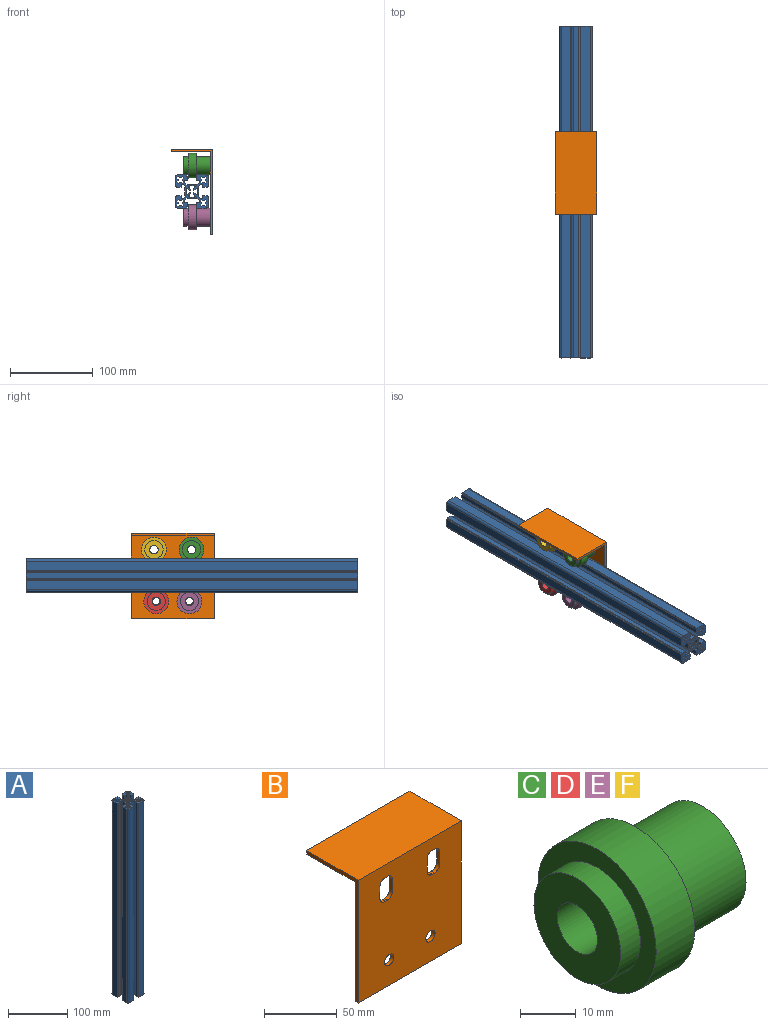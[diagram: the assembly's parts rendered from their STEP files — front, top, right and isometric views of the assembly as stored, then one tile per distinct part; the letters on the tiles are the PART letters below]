
ASSEMBLY  parts=6 mates=5
PART A: 178 faces, bbox 40x40x400 mm
  f0: cylinder r=2.77mm len=400mm, axis (0,0,1), area 706.3mm2, adj f1,f2,f176,f177
  f1: plane 400x1.43mm, normal (0.71,0.71,0), area 809.2mm2, adj f0,f175,f176,f177
  f2: plane 400x1.43mm, normal (0.71,-0.71,0), area 808.9mm2, adj f0,f163,f176,f177
  f3: cylinder r=3mm len=400mm, axis (0,0,1), area 1885mm2, adj f4,f82,f176,f177
  f4: plane 400x10.93mm, normal (-1,0,0), area 4370mm2, adj f3,f9,f176,f177
  f5: plane 400x3.65mm, normal (1,0,0), area 1460mm2, adj f6,f7,f176,f177
  f6: plane 400x2.46mm, normal (0,-1,0), area 984.8mm2, adj f5,f10,f176,f177
  f7: plane 400x5.5mm, normal (0,-1,0), area 2200mm2, adj f5,f8,f176,f177
  f8: plane 400x0.98mm, normal (-1,0,0), area 390mm2, adj f7,f9,f176,f177
  f9: plane 400x1.5mm, normal (0,-1,0), area 600mm2, adj f4,f8,f176,f177
  f10: plane 400x2.83mm, normal (-0.71,-0.71,0), area 1598.1mm2, adj f6,f11,f176,f177
  f11: cylinder r=0.5mm len=400mm, axis (0,0,1), area 325.2mm2, adj f10,f12,f176,f177
  f12: cylinder r=2.3mm len=400mm, axis (0,0,1), area 774mm2, adj f11,f13,f176,f177
  f13: plane 400x6.97mm, normal (-1,0,0), area 2787.1mm2, adj f12,f14,f176,f177
  f14: cylinder r=2.3mm len=400mm, axis (0,0,1), area 774mm2, adj f13,f15,f176,f177
  f15: cylinder r=0.5mm len=400mm, axis (0,0,1), area 325.1mm2, adj f14,f16,f176,f177
  f16: plane 400x2.83mm, normal (-0.71,0.71,0), area 1598.4mm2, adj f15,f17,f176,f177
  f17: plane 400x2.46mm, normal (0,1,0), area 984.8mm2, adj f16,f18,f176,f177
  f18: plane 400x3.65mm, normal (1,0,0), area 1460mm2, adj f17,f19,f176,f177
  f19: plane 400x5.5mm, normal (0,1,0), area 2200mm2, adj f18,f20,f176,f177
  f20: plane 400x0.98mm, normal (-1,0,0), area 390mm2, adj f19,f21,f176,f177
  f21: plane 400x1.5mm, normal (0,1,0), area 600mm2, adj f20,f22,f176,f177
  f22: plane 400x10.93mm, normal (-1,0,0), area 4370mm2, adj f21,f23,f176,f177
  f23: cylinder r=3mm len=400mm, axis (0,0,1), area 1885mm2, adj f22,f24,f176,f177
  f24: plane 400x10.93mm, normal (0,-1,0), area 4370mm2, adj f23,f25,f176,f177
  f25: plane 400x1.5mm, normal (1,0,0), area 600mm2, adj f24,f26,f176,f177
  f26: plane 400x0.98mm, normal (0,-1,0), area 390mm2, adj f25,f27,f176,f177
  f27: plane 400x5.5mm, normal (1,0,0), area 2200mm2, adj f26,f28,f176,f177
  f28: plane 400x3.65mm, normal (0,1,0), area 1460mm2, adj f27,f29,f176,f177
  f29: plane 400x2.46mm, normal (1,0,0), area 985.2mm2, adj f28,f30,f176,f177
  f30: plane 400x2.83mm, normal (0.71,-0.71,0), area 1598.1mm2, adj f29,f31,f176,f177
  f31: cylinder r=0.5mm len=400mm, axis (0,0,1), area 325.2mm2, adj f30,f32,f176,f177
  f32: cylinder r=2.3mm len=400mm, axis (0,0,1), area 774.5mm2, adj f31,f33,f176,f177
  f33: plane 400x6.97mm, normal (0,-1,0), area 2786.4mm2, adj f32,f34,f176,f177
  f34: cylinder r=2.3mm len=400mm, axis (0,0,1), area 774.5mm2, adj f33,f35,f176,f177
  f35: cylinder r=0.5mm len=400mm, axis (0,0,1), area 325.4mm2, adj f34,f36,f176,f177
  f36: plane 400x2.83mm, normal (-0.71,-0.71,0), area 1598.3mm2, adj f35,f37,f176,f177
  f37: plane 400x2.46mm, normal (-1,0,0), area 985.2mm2, adj f36,f38,f176,f177
  f38: plane 400x3.65mm, normal (0,1,0), area 1460mm2, adj f37,f39,f176,f177
  f39: plane 400x5.5mm, normal (-1,0,0), area 2200mm2, adj f38,f40,f176,f177
  f40: plane 400x0.98mm, normal (0,-1,0), area 390mm2, adj f39,f41,f176,f177
  f41: plane 400x1.5mm, normal (-1,0,0), area 600mm2, adj f40,f42,f176,f177
  f42: plane 400x10.93mm, normal (0,-1,0), area 4370mm2, adj f41,f43,f176,f177
  f43: cylinder r=3mm len=400mm, axis (0,0,1), area 1885mm2, adj f42,f44,f176,f177
  f44: plane 400x10.93mm, normal (1,0,0), area 4370mm2, adj f43,f45,f176,f177
  f45: plane 400x1.5mm, normal (0,1,0), area 600mm2, adj f44,f46,f176,f177
  f46: plane 400x0.98mm, normal (1,0,0), area 390mm2, adj f45,f47,f176,f177
  f47: plane 400x5.5mm, normal (0,1,0), area 2200mm2, adj f46,f48,f176,f177
  f48: plane 400x3.65mm, normal (-1,0,0), area 1460mm2, adj f47,f49,f176,f177
  f49: plane 400x2.46mm, normal (0,1,0), area 984.8mm2, adj f48,f50,f176,f177
  f50: plane 400x2.83mm, normal (0.71,0.71,0), area 1598.3mm2, adj f49,f51,f176,f177
  f51: cylinder r=0.5mm len=400mm, axis (0,0,1), area 325.4mm2, adj f50,f52,f176,f177
  f52: cylinder r=2.3mm len=400mm, axis (0,0,1), area 774mm2, adj f51,f53,f176,f177
  f53: plane 400x6.97mm, normal (1,0,0), area 2787.1mm2, adj f52,f54,f176,f177
  f54: cylinder r=2.3mm len=400mm, axis (0,0,1), area 774mm2, adj f53,f55,f176,f177
  f55: cylinder r=0.5mm len=400mm, axis (0,0,1), area 325.5mm2, adj f54,f56,f176,f177
  f56: plane 400x2.83mm, normal (0.71,-0.71,0), area 1598mm2, adj f55,f57,f176,f177
  f57: plane 400x2.46mm, normal (0,-1,0), area 984.8mm2, adj f56,f58,f176,f177
  f58: plane 400x3.65mm, normal (-1,0,0), area 1460mm2, adj f57,f59,f176,f177
  f59: plane 400x5.5mm, normal (0,-1,0), area 2200mm2, adj f58,f60,f176,f177
  f60: plane 400x0.98mm, normal (1,0,0), area 390mm2, adj f59,f61,f176,f177
  f61: plane 400x1.5mm, normal (0,-1,0), area 600mm2, adj f60,f62,f176,f177
  f62: plane 400x10.93mm, normal (1,0,0), area 4370mm2, adj f61,f63,f176,f177
  f63: cylinder r=3mm len=400mm, axis (0,0,1), area 1885mm2, adj f62,f64,f176,f177
  f64: plane 400x10.93mm, normal (0,1,0), area 4370mm2, adj f63,f65,f176,f177
  f65: plane 400x1.5mm, normal (-1,0,0), area 600mm2, adj f64,f66,f176,f177
  f66: plane 400x0.98mm, normal (0,1,0), area 390mm2, adj f65,f67,f176,f177
  f67: plane 400x5.5mm, normal (-1,0,0), area 2200mm2, adj f66,f68,f176,f177
  f68: plane 400x3.65mm, normal (0,-1,0), area 1460mm2, adj f67,f69,f176,f177
  f69: plane 400x2.46mm, normal (-1,0,0), area 984.8mm2, adj f68,f70,f176,f177
  f70: plane 400x2.83mm, normal (-0.71,0.71,0), area 1598.3mm2, adj f69,f71,f176,f177
  f71: cylinder r=0.5mm len=400mm, axis (0,0,1), area 325.4mm2, adj f70,f72,f176,f177
  f72: cylinder r=2.3mm len=400mm, axis (0,0,1), area 774mm2, adj f71,f73,f176,f177
  f73: plane 400x6.97mm, normal (0,1,0), area 2787.1mm2, adj f72,f74,f176,f177
  f74: cylinder r=2.3mm len=400mm, axis (0,0,1), area 774mm2, adj f73,f75,f176,f177
  f75: cylinder r=0.5mm len=400mm, axis (0,0,1), area 325.2mm2, adj f74,f76,f176,f177
  f76: plane 400x2.83mm, normal (0.71,0.71,0), area 1598.1mm2, adj f75,f77,f176,f177
  f77: plane 400x2.46mm, normal (1,0,0), area 984.8mm2, adj f76,f78,f176,f177
  f78: plane 400x3.65mm, normal (0,-1,0), area 1460mm2, adj f77,f79,f176,f177
  f79: plane 400x5.5mm, normal (1,0,0), area 2200mm2, adj f78,f80,f176,f177
  f80: plane 400x0.98mm, normal (0,1,0), area 390mm2, adj f79,f81,f176,f177
  f81: plane 400x1.5mm, normal (1,0,0), area 600mm2, adj f80,f82,f176,f177
  f82: plane 400x10.93mm, normal (0,1,0), area 4370mm2, adj f3,f81,f176,f177
  f83: plane 400x1.77mm, normal (0.71,0.71,0), area 999.8mm2, adj f84,f98,f176,f177
  f84: plane 400x1.43mm, normal (-0.71,0.71,0), area 808.9mm2, adj f83,f85,f176,f177
  f85: cylinder r=2.77mm len=400mm, axis (0,0,1), area 706.3mm2, adj f84,f86,f176,f177
  f86: plane 400x1.43mm, normal (0.71,0.71,0), area 808.9mm2, adj f85,f87,f176,f177
  f87: plane 400x1.77mm, normal (-0.71,0.71,0), area 999.8mm2, adj f86,f88,f176,f177
  f88: plane 400x1.43mm, normal (-0.71,-0.71,0), area 808.9mm2, adj f87,f89,f176,f177
  f89: cylinder r=2.77mm len=400mm, axis (0,0,1), area 706.3mm2, adj f88,f90,f176,f177
  f90: plane 400x1.43mm, normal (-0.71,0.71,0), area 809.2mm2, adj f89,f91,f176,f177
  f91: plane 400x1.77mm, normal (-0.71,-0.71,0), area 999.8mm2, adj f90,f92,f176,f177
  f92: plane 400x1.43mm, normal (0.71,-0.71,0), area 808.9mm2, adj f91,f93,f176,f177
  f93: cylinder r=2.77mm len=400mm, axis (0,0,1), area 706.3mm2, adj f92,f94,f176,f177
  f94: plane 400x1.43mm, normal (-0.71,-0.71,0), area 808.9mm2, adj f93,f95,f176,f177
  f95: plane 400x1.77mm, normal (0.71,-0.71,0), area 999.8mm2, adj f94,f96,f176,f177
  f96: plane 400x1.43mm, normal (0.71,0.71,0), area 809.2mm2, adj f95,f97,f176,f177
  f97: cylinder r=2.77mm len=400mm, axis (0,0,1), area 706.3mm2, adj f96,f98,f176,f177
  f98: plane 400x1.43mm, normal (0.71,-0.71,0), area 808.9mm2, adj f83,f97,f176,f177
  f99: plane 400x1.77mm, normal (0.71,0.71,0), area 999.8mm2, adj f100,f114,f176,f177
  f100: plane 400x1.43mm, normal (-0.71,0.71,0), area 808.9mm2, adj f99,f101,f176,f177
  f101: cylinder r=2.77mm len=400mm, axis (0,0,1), area 706.3mm2, adj f100,f102,f176,f177
  f102: plane 400x1.43mm, normal (0.71,0.71,0), area 808.9mm2, adj f101,f103,f176,f177
  f103: plane 400x1.77mm, normal (-0.71,0.71,0), area 999.8mm2, adj f102,f104,f176,f177
  f104: plane 400x1.43mm, normal (-0.71,-0.71,0), area 808.9mm2, adj f103,f105,f176,f177
  f105: cylinder r=2.77mm len=400mm, axis (0,0,1), area 706.3mm2, adj f104,f106,f176,f177
  f106: plane 400x1.43mm, normal (-0.71,0.71,0), area 809.2mm2, adj f105,f107,f176,f177
  f107: plane 400x1.77mm, normal (-0.71,-0.71,0), area 999.8mm2, adj f106,f108,f176,f177
  f108: plane 400x1.43mm, normal (0.71,-0.71,0), area 808.9mm2, adj f107,f109,f176,f177
  f109: cylinder r=2.77mm len=400mm, axis (0,0,1), area 706.3mm2, adj f108,f110,f176,f177
  f110: plane 400x1.43mm, normal (-0.71,-0.71,0), area 808.9mm2, adj f109,f111,f176,f177
  f111: plane 400x1.77mm, normal (0.71,-0.71,0), area 999.8mm2, adj f110,f112,f176,f177
  f112: plane 400x1.43mm, normal (0.71,0.71,0), area 809.2mm2, adj f111,f113,f176,f177
  f113: cylinder r=2.77mm len=400mm, axis (0,0,1), area 706.3mm2, adj f112,f114,f176,f177
  f114: plane 400x1.43mm, normal (0.71,-0.71,0), area 808.9mm2, adj f99,f113,f176,f177
  f115: cylinder r=1mm len=400mm, axis (0,0,1), area 942.5mm2, adj f116,f146,f176,f177
  f116: plane 400x0.99mm, normal (-0.71,0.71,0), area 560mm2, adj f115,f117,f176,f177
  f117: plane 400x1.58mm, normal (-0.57,0.82,0), area 769.1mm2, adj f116,f118,f176,f177
  f118: cylinder r=2.77mm len=400mm, axis (0,0,1), area 621mm2, adj f117,f119,f176,f177
  f119: plane 400x1.58mm, normal (0.82,-0.57,0), area 769.1mm2, adj f118,f120,f176,f177
  f120: plane 400x0.99mm, normal (0.71,-0.71,0), area 560.5mm2, adj f119,f121,f176,f177
  f121: cylinder r=1mm len=400mm, axis (0,0,1), area 942.5mm2, adj f120,f122,f176,f177
  f122: plane 400x5.46mm, normal (0,1,0), area 2184.6mm2, adj f121,f123,f176,f177
  f123: cylinder r=1mm len=400mm, axis (0,0,1), area 942.5mm2, adj f122,f124,f176,f177
  f124: plane 400x0.99mm, normal (-0.71,-0.71,0), area 560.5mm2, adj f123,f125,f176,f177
  f125: plane 400x1.58mm, normal (-0.82,-0.57,0), area 769.1mm2, adj f124,f126,f176,f177
  f126: cylinder r=2.77mm len=400mm, axis (0,0,1), area 620.7mm2, adj f125,f127,f176,f177
  f127: plane 400x1.58mm, normal (0.57,0.82,0), area 769.5mm2, adj f126,f128,f176,f177
  f128: plane 400x0.99mm, normal (0.71,0.71,0), area 560mm2, adj f127,f129,f176,f177
  f129: cylinder r=1mm len=400mm, axis (0,0,1), area 942.5mm2, adj f128,f130,f176,f177
  f130: plane 400x5.46mm, normal (-1,0,0), area 2184.2mm2, adj f129,f131,f176,f177
  f131: cylinder r=1mm len=400mm, axis (0,0,1), area 942.5mm2, adj f130,f132,f176,f177
  f132: plane 400x0.99mm, normal (0.71,-0.71,0), area 560mm2, adj f131,f133,f176,f177
  f133: plane 400x1.58mm, normal (0.57,-0.82,0), area 769.5mm2, adj f132,f134,f176,f177
  f134: cylinder r=2.77mm len=400mm, axis (0,0,1), area 620.7mm2, adj f133,f135,f176,f177
  f135: plane 400x1.58mm, normal (-0.82,0.57,0), area 769.1mm2, adj f134,f136,f176,f177
  f136: plane 400x0.99mm, normal (-0.71,0.71,0), area 560mm2, adj f135,f137,f176,f177
  f137: cylinder r=1mm len=400mm, axis (0,0,1), area 942.5mm2, adj f136,f138,f176,f177
  f138: plane 400x5.46mm, normal (0,-1,0), area 2183.8mm2, adj f137,f139,f176,f177
  f139: cylinder r=1mm len=400mm, axis (0,0,1), area 942.5mm2, adj f138,f140,f176,f177
  f140: plane 400x0.99mm, normal (0.71,0.71,0), area 560mm2, adj f139,f141,f176,f177
  f141: plane 400x1.58mm, normal (0.82,0.57,0), area 769.1mm2, adj f140,f142,f176,f177
  f142: cylinder r=2.77mm len=400mm, axis (0,0,1), area 621mm2, adj f141,f143,f176,f177
  f143: plane 400x1.58mm, normal (-0.57,-0.82,0), area 769.1mm2, adj f142,f144,f176,f177
  f144: plane 400x0.99mm, normal (-0.71,-0.71,0), area 560mm2, adj f143,f145,f176,f177
  f145: cylinder r=1mm len=400mm, axis (0,0,1), area 942.5mm2, adj f144,f146,f176,f177
  f146: plane 400x5.46mm, normal (1,0,0), area 2184.2mm2, adj f115,f145,f176,f177
  f147: plane 400x1.43mm, normal (0.71,0.71,0), area 809.2mm2, adj f148,f162,f176,f177
  f148: cylinder r=2.77mm len=400mm, axis (0,0,1), area 706.3mm2, adj f147,f149,f176,f177
  f149: plane 400x1.43mm, normal (0.71,-0.71,0), area 808.9mm2, adj f148,f150,f176,f177
  f150: plane 400x1.77mm, normal (0.71,0.71,0), area 999.8mm2, adj f149,f151,f176,f177
  f151: plane 400x1.43mm, normal (-0.71,0.71,0), area 808.9mm2, adj f150,f152,f176,f177
  f152: cylinder r=2.77mm len=400mm, axis (0,0,1), area 706.3mm2, adj f151,f153,f176,f177
  f153: plane 400x1.43mm, normal (0.71,0.71,0), area 808.9mm2, adj f152,f154,f176,f177
  f154: plane 400x1.77mm, normal (-0.71,0.71,0), area 999.8mm2, adj f153,f155,f176,f177
  f155: plane 400x1.43mm, normal (-0.71,-0.71,0), area 808.9mm2, adj f154,f156,f176,f177
  f156: cylinder r=2.77mm len=400mm, axis (0,0,1), area 706.3mm2, adj f155,f157,f176,f177
  f157: plane 400x1.43mm, normal (-0.71,0.71,0), area 809.2mm2, adj f156,f158,f176,f177
  f158: plane 400x1.77mm, normal (-0.71,-0.71,0), area 999.8mm2, adj f157,f159,f176,f177
  f159: plane 400x1.43mm, normal (0.71,-0.71,0), area 808.9mm2, adj f158,f160,f176,f177
  f160: cylinder r=2.77mm len=400mm, axis (0,0,1), area 706.3mm2, adj f159,f161,f176,f177
  f161: plane 400x1.43mm, normal (-0.71,-0.71,0), area 808.9mm2, adj f160,f162,f176,f177
  f162: plane 400x1.77mm, normal (0.71,-0.71,0), area 999.8mm2, adj f147,f161,f176,f177
  f163: plane 400x1.77mm, normal (0.71,0.71,0), area 999.8mm2, adj f2,f164,f176,f177
  f164: plane 400x1.43mm, normal (-0.71,0.71,0), area 808.9mm2, adj f163,f165,f176,f177
  f165: cylinder r=2.77mm len=400mm, axis (0,0,1), area 706.3mm2, adj f164,f166,f176,f177
  f166: plane 400x1.43mm, normal (0.71,0.71,0), area 808.9mm2, adj f165,f167,f176,f177
  f167: plane 400x1.77mm, normal (-0.71,0.71,0), area 999.8mm2, adj f166,f168,f176,f177
  f168: plane 400x1.43mm, normal (-0.71,-0.71,0), area 808.9mm2, adj f167,f169,f176,f177
  f169: cylinder r=2.77mm len=400mm, axis (0,0,1), area 706.3mm2, adj f168,f170,f176,f177
  f170: plane 400x1.43mm, normal (-0.71,0.71,0), area 809.2mm2, adj f169,f171,f176,f177
  f171: plane 400x1.77mm, normal (-0.71,-0.71,0), area 999.8mm2, adj f170,f172,f176,f177
  f172: plane 400x1.43mm, normal (0.71,-0.71,0), area 808.9mm2, adj f171,f173,f176,f177
  f173: cylinder r=2.77mm len=400mm, axis (0,0,1), area 706.3mm2, adj f172,f174,f176,f177
  f174: plane 400x1.43mm, normal (-0.71,-0.71,0), area 808.9mm2, adj f173,f175,f176,f177
  f175: plane 400x1.77mm, normal (0.71,-0.71,0), area 999.8mm2, adj f1,f174,f176,f177
  f176: plane 40x40mm, normal (0,0,1), area 698.5mm2, adj f0,f1,f2,f3,f4,f5,f6,f7
  f177: plane 40x40mm, normal (0,0,-1), area 698.5mm2, adj f0,f1,f2,f3,f4,f5,f6,f7
PART B: 26 faces, bbox 100x50x103 mm
  f0: plane 103x100mm, normal (0,-1,0), area 9727.7mm2, adj f2,f5,f6,f7,f8,f9,f10,f11
  f1: plane 100x100mm, normal (0,1,0), area 9427.7mm2, adj f2,f3,f6,f7,f8,f9,f10,f11
  f2: plane 100x3mm, normal (0,0,-1), area 300mm2, adj f0,f1,f6,f7
  f3: plane 100x47mm, normal (0,0,-1), area 4700mm2, adj f1,f4,f6,f7
  f4: plane 100x3mm, normal (0,1,0), area 300mm2, adj f3,f5,f6,f7
  f5: plane 100x50mm, normal (0,0,1), area 5000mm2, adj f0,f4,f6,f7
  f6: plane 103x50mm, normal (1,0,0), area 450mm2, adj f0,f1,f2,f3,f4,f5
  f7: plane 103x50mm, normal (-1,0,0), area 450mm2, adj f0,f1,f2,f3,f4,f5
  f8: plane 3x2.2mm, normal (0,0,-1), area 6.6mm2, adj f0,f1,f9,f15
  f9: cylinder r=5mm len=5mm, axis (0,-1,0), area 23.6mm2, adj f0,f1,f8,f10
  f10: plane 10x3mm, normal (1,0,0), area 30mm2, adj f0,f1,f9,f11
  f11: cylinder r=5mm len=5mm, axis (0,-1,0), area 23.6mm2, adj f0,f1,f10,f12
  f12: plane 3x2.2mm, normal (0,0,1), area 6.6mm2, adj f0,f1,f11,f13
  f13: cylinder r=5mm len=5mm, axis (0,-1,0), area 23.6mm2, adj f0,f1,f12,f14
  f14: plane 10x3mm, normal (-1,0,0), area 30mm2, adj f0,f1,f13,f15
  f15: cylinder r=5mm len=5mm, axis (0,-1,0), area 23.6mm2, adj f0,f1,f8,f14
  f16: cylinder r=5mm len=5mm, axis (0,-1,0), area 23.6mm2, adj f0,f1,f17,f23
  f17: plane 10x3mm, normal (1,0,0), area 30mm2, adj f0,f1,f16,f18
  f18: cylinder r=5mm len=5mm, axis (0,-1,0), area 23.6mm2, adj f0,f1,f17,f19
  f19: plane 3x2.2mm, normal (0,0,1), area 6.6mm2, adj f0,f1,f18,f20
  f20: cylinder r=5mm len=5mm, axis (0,-1,0), area 23.6mm2, adj f0,f1,f19,f21
  f21: plane 10x3mm, normal (-1,0,0), area 30mm2, adj f0,f1,f20,f22
  f22: cylinder r=5mm len=5mm, axis (0,-1,0), area 23.6mm2, adj f0,f1,f21,f23
  f23: plane 3x2.2mm, normal (0,0,-1), area 6.6mm2, adj f0,f1,f16,f22
  f24: cylinder r=4.5mm len=9mm, axis (0,-1,0), area 84.8mm2, adj f0,f1
  f25: cylinder r=4.5mm len=9mm, axis (0,-1,0), area 84.8mm2, adj f0,f1
PART C: 8 faces, bbox 31.8x30x30 mm
  f0: cylinder r=11mm len=22mm, axis (-1,0,0), area 1175mm2, adj f1,f6
  f1: plane 30x30mm, normal (1,0,0), area 326.7mm2, adj f0,f2
  f2: cylinder r=15mm len=30mm, axis (-1,0,0), area 923.6mm2, adj f1,f3
  f3: plane 30x30mm, normal (-1,0,0), area 326.7mm2, adj f2,f4
  f4: cylinder r=11mm len=22mm, axis (-1,0,0), area 345.6mm2, adj f3,f5
  f5: plane 22x22mm, normal (-1,0,0), area 298.4mm2, adj f4,f7
  f6: plane 22x22mm, normal (1,0,0), area 298.4mm2, adj f0,f7
  f7: cylinder r=5.1mm len=31.8mm, axis (1,0,0), area 1019mm2, adj f5,f6
PART D: same geometry as C
PART E: same geometry as C
PART F: same geometry as C
PLACE A rot(axis=(1,0,0),90deg) t=(50.59,182.59,-13.97)mm
PLACE B rot(axis=(0,0,1),90deg) t=(385.01,-44.32,251.44)mm
PLACE C rot(axis=(0,0,-1),0deg) t=(58.36,-16.85,35.34)mm
PLACE D rot(axis=(0,0,-1),0deg) t=(58.36,25.68,-26.89)mm
PLACE E rot(axis=(0,0,-1),0deg) t=(58.36,-14.32,-27.05)mm
PLACE F rot(axis=(0,0,-1),0deg) t=(58.36,28.45,35.17)mm
MATE planar C.f0 <-> A.f67  axis (1,0,0) through (55.69,-16.85,17.25)mm
MATE planar D.f0 <-> B.f24  axis (1,0,0) through (72.69,25.68,-44.98)mm
MATE planar F.f0 <-> B.f1  axis (1,0,0) through (72.69,28.45,17.08)mm
MATE planar E.f0 <-> B.f25  axis (1,0,0) through (72.69,-14.32,-45.14)mm
MATE planar B.f1 <-> C.f0  axis (-1,0,0) through (72.69,5.68,-17.18)mm
